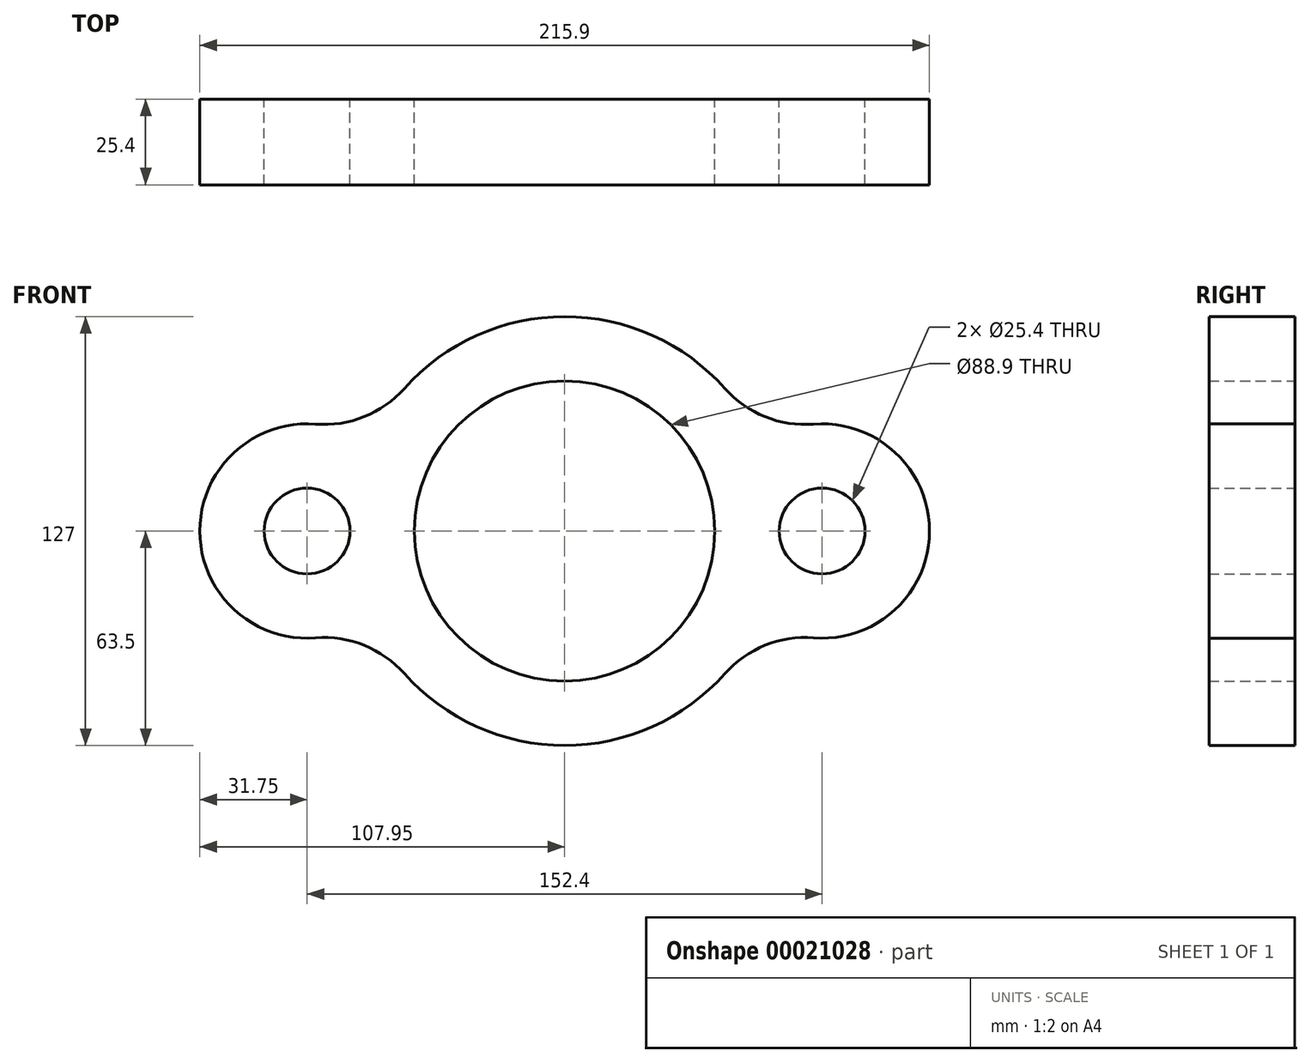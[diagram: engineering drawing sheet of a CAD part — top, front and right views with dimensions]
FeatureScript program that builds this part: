
annotation { "Feature Type Name" : "Feature", "Feature Type Description" : "" }
export const myFeature = defineFeature(function(context is Context, id is Id, definition is map)
    precondition{}
    {
        {
            var Q0;
            Q0=qCreatedBy(makeId("Front.planeOp"),FACE);
            var sketch = newSketch(context, id + "F0", { "sketchPlane" : qUnion([Q0])});
            skCircle(sketch, "E0", {"center": v(0, 0) * mm, "radius": 44.45 * mm});
            skCircle(sketch, "E1", {"center": v(-76.2, 0) * mm, "radius": 12.7 * mm});
            skCircle(sketch, "E2", {"center": v(76.2, 0) * mm, "radius": 12.7 * mm});
            skCircle(sketch, "E3", {"center": v(0, 0) * mm, "radius": 63.5 * mm});
            skCircle(sketch, "E4", {"center": v(76.2, 0) * mm, "radius": 31.75 * mm});
            skCircle(sketch, "E5", {"center": v(-76.2, 0) * mm, "radius": 31.75 * mm});
            skArc(sketch, "E6", {"start": v(47.45, 42.2) * mm, "mid": v(59.33, 33.84) * mm, "end": v(73.69, 31.65) * mm});
            skArc(sketch, "E7", {"start": v(-73.69, 31.65) * mm, "mid": v(-59.33, 33.84) * mm, "end": v(-47.45, 42.2) * mm});
            skArc(sketch, "E8", {"start": v(73.69, -31.65) * mm, "mid": v(59.33, -33.84) * mm, "end": v(47.45, -42.2) * mm});
            skArc(sketch, "E9", {"start": v(-47.45, -42.2) * mm, "mid": v(-59.33, -33.84) * mm, "end": v(-73.69, -31.65) * mm});
            skSolve(sketch);
        }
        {
            var Q0;
            Q0 = qSketchRegion(id + "F0", true);
            var Q1;
            {var subQ1=sQuery(id+"F0.wireOp",EDGE,"E3");var subQ5=makeQuery(id+"F0.imprint","INTERSECT",VERTEX,{"derivedFrom":[sQuery(id+"F0.wireOp",EDGE,"E1"),subQ1]});Q1=makeQuery(id+"F0.imprint","IMPRINT",FACE,{"disambiguationData":[TD([[makeQuery(id+"F0.imprint","IMPRINT",EDGE,{"disambiguationData":[TD([[subQ5,1.0]])],"derivedFrom":subQ1}),1.0]])]});}
            var Q2;
            {var subQ1=sQuery(id+"F0.wireOp",EDGE,"E3");var subQ5=makeQuery(id+"F0.imprint","INTERSECT",VERTEX,{"derivedFrom":[sQuery(id+"F0.wireOp",EDGE,"E2"),subQ1]});Q2=makeQuery(id+"F0.imprint","IMPRINT",FACE,{"disambiguationData":[TD([[makeQuery(id+"F0.imprint","IMPRINT",EDGE,{"disambiguationData":[TD([[subQ5,-1.0]])],"derivedFrom":subQ1}),1.0]])]});}
            extrude(context, id + "F1", {"entities" : qUnion([Q0, Q1, Q2]), "depth" : 25.4 * mm});
        }
    });
